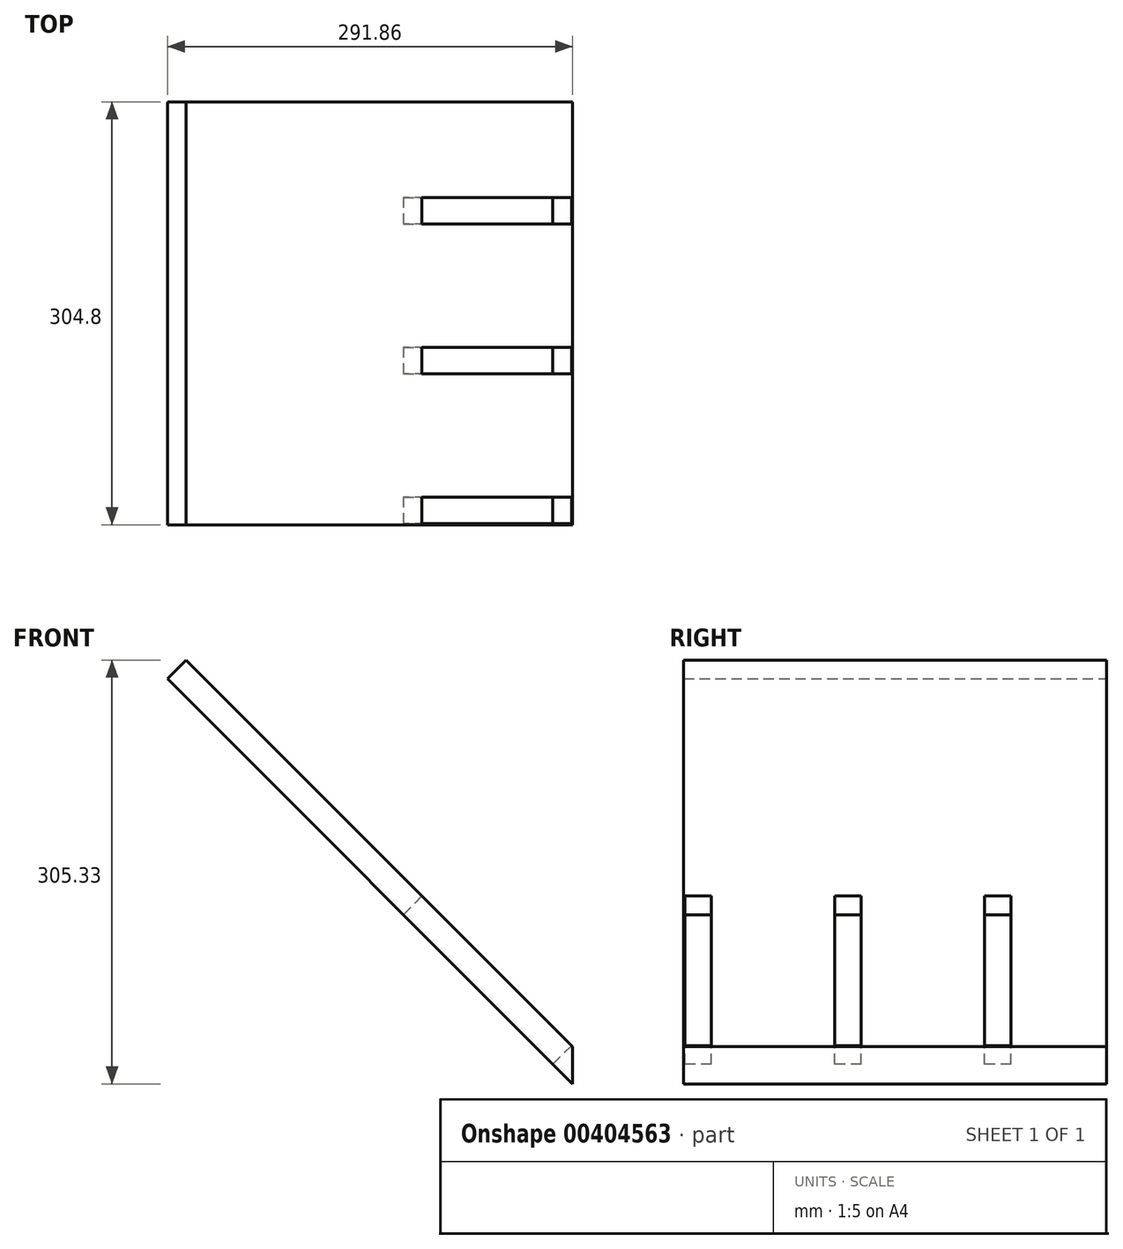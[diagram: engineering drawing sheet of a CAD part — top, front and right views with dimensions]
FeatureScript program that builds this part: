
annotation { "Feature Type Name" : "Feature", "Feature Type Description" : "" }
export const myFeature = defineFeature(function(context is Context, id is Id, definition is map)
    precondition{}
    {
        {
            var Q0;
            Q0=qCreatedBy(makeId("Front.planeOp"),FACE);
            var sketch = newSketch(context, id + "F0", { "sketchPlane" : qUnion([Q0])});
            skLineSegment(sketch, "E0.MirrorCS", {"start": v(378.53, 134.65) * mm, "end": v(86.67, 426.5) * mm});
            skLineSegment(sketch, "E1.MirrorCS", {"start": v(378.53, 161.6) * mm, "end": v(100.14, 439.98) * mm});
            skLineSegment(sketch, "E2.MirrorCS", {"start": v(378.53, 134.65) * mm, "end": v(378.53, 161.6) * mm});
            skLineSegment(sketch, "E3", {"start": v(100.14, 439.98) * mm, "end": v(86.67, 426.5) * mm});
            skSolve(sketch);
        }
        {
            var Q0;
            Q0=qSketchRegion(id+"F0",true);
            extrude(context, id + "F1", {"entities" : qUnion([Q0]), "endBound" : BoundingType.SYMMETRIC, "depth" : 304.8 * mm});
        }
        {
            var Q0;
            Q0=makeQuery(id+"F1.opExtrude","SWEPT_FACE",FACE,{"disambiguationData":[OSD([sQuery(id+"F0.wireOp",EDGE,"E1.MirrorCS")])]});
            var sketch = newSketch(context, id + "F2", { "sketchPlane" : qUnion([Q0])});
            skLineSegment(sketch, "E4.bottom", {"start": v(83.55, -152.4) * mm, "end": v(64.5, -152.4) * mm});
            skLineSegment(sketch, "E4.top", {"start": v(83.55, 0) * mm, "end": v(64.5, 0) * mm});
            skLineSegment(sketch, "E4.left", {"start": v(83.55, -152.4) * mm, "end": v(83.55, 0) * mm});
            skLineSegment(sketch, "E4.right", {"start": v(64.5, -152.4) * mm, "end": v(64.5, 0) * mm});
            skLineSegment(sketch, "E5.bottom", {"start": v(-24.4, -152.4) * mm, "end": v(-43.45, -152.4) * mm});
            skLineSegment(sketch, "E5.top", {"start": v(-24.4, 0) * mm, "end": v(-43.45, 0) * mm});
            skLineSegment(sketch, "E5.left", {"start": v(-24.4, -152.4) * mm, "end": v(-24.4, 0) * mm});
            skLineSegment(sketch, "E5.right", {"start": v(-43.45, -152.4) * mm, "end": v(-43.45, 0) * mm});
            skLineSegment(sketch, "E6.bottom", {"start": v(-132.35, -152.4) * mm, "end": v(-151.4, -152.4) * mm});
            skLineSegment(sketch, "E6.top", {"start": v(-132.35, 0) * mm, "end": v(-151.4, 0) * mm});
            skLineSegment(sketch, "E6.left", {"start": v(-132.35, -152.4) * mm, "end": v(-132.35, 0) * mm});
            skLineSegment(sketch, "E6.right", {"start": v(-151.4, -152.4) * mm, "end": v(-151.4, 0) * mm});
            skSolve(sketch);
        }
        {
            var Q0;
            Q0=qSketchRegion(id+"F2",true);
            extrude(context, id + "F3", {"entities" : qUnion([Q0]), "operationType" : NewBodyOperationType.REMOVE, "oppositeDirection" : true, "depth" : 19.05 * mm});
        }
    });
